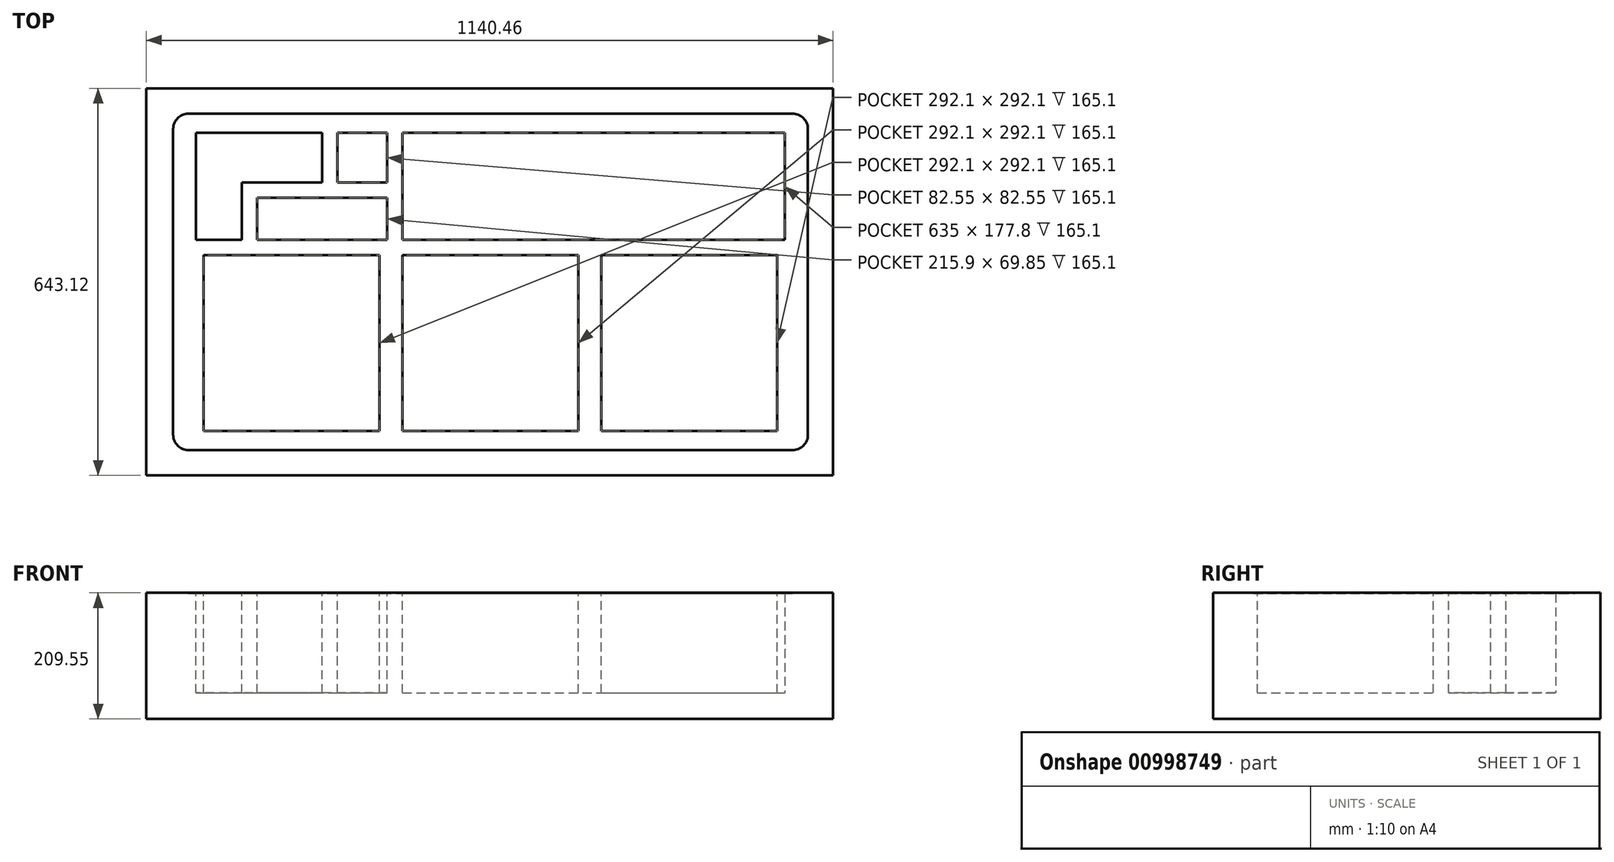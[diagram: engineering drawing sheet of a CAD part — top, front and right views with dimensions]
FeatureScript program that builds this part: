
annotation { "Feature Type Name" : "Feature", "Feature Type Description" : "" }
export const myFeature = defineFeature(function(context is Context, id is Id, definition is map)
    precondition{}
    {
        {
            var Q0;
            Q0=qCreatedBy(makeId("Top.planeOp"),FACE);
            var sketch = newSketch(context, id + "F0", { "sketchPlane" : qUnion([Q0])});
            skLineSegment(sketch, "E0.bottom", {"start": v(-44.45, -42.16) * mm, "end": v(1096, -42.16) * mm});
            skLineSegment(sketch, "E0.top", {"start": v(-44.45, 600.96) * mm, "end": v(1096, 600.96) * mm});
            skLineSegment(sketch, "E0.left", {"start": v(-44.45, -42.16) * mm, "end": v(-44.45, 600.96) * mm});
            skLineSegment(sketch, "E0.right", {"start": v(1096, -42.16) * mm, "end": v(1096, 600.96) * mm});
            skSolve(sketch);
        }
        {
            var Q0;
            Q0=makeQuery(id+"F0.imprint","IMPRINT",FACE,{"disambiguationData":[TD([[makeQuery(id+"F0.imprint","IMPRINT",EDGE,{"derivedFrom":sQuery(id+"F0.wireOp",EDGE,"E0.bottom")}),1.0]])]});
            extrude(context, id + "F1", {"entities" : qUnion([Q0]), "depth" : 209.55 * mm, "offsetDistance" : 25.4 * mm});
        }
        {
            var Q0;
            Q0=makeQuery(id+"F1.opExtrude","CAP_FACE",FACE,{"disambiguationData":[OSD([sQuery(id+"F0.wireOp",EDGE,"E0.bottom"),sQuery(id+"F0.wireOp",EDGE,"E0.top"),sQuery(id+"F0.wireOp",EDGE,"E0.left"),sQuery(id+"F0.wireOp",EDGE,"E0.right")])],"isStart":false});
            var sketch = newSketch(context, id + "F2", { "sketchPlane" : qUnion([Q0])});
            skLineSegment(sketch, "E1.bottom", {"start": v(25.4, 0) * mm, "end": v(1028.7, 0) * mm});
            skLineSegment(sketch, "E1.top", {"start": v(25.4, 558.8) * mm, "end": v(1028.7, 558.8) * mm});
            skLineSegment(sketch, "E1.left", {"start": v(0, 25.4) * mm, "end": v(0, 533.4) * mm});
            skLineSegment(sketch, "E1.right", {"start": v(1054.1, 25.4) * mm, "end": v(1054.1, 533.4) * mm});
            skPoint(sketch, "E2.visualSharp", {"position": v(0, 558.8) * mm});
            skArc(sketch, "E2.filletArc", {"start": v(25.4, 558.8) * mm, "mid": v(7.44, 551.36) * mm, "end": v(0, 533.4) * mm});
            skPoint(sketch, "E3.visualSharp", {"position": v(1054.1, 558.8) * mm});
            skArc(sketch, "E3.filletArc", {"start": v(1054.1, 533.4) * mm, "mid": v(1046.66, 551.36) * mm, "end": v(1028.7, 558.8) * mm});
            skPoint(sketch, "E4.visualSharp", {"position": v(1054.1, 0) * mm});
            skArc(sketch, "E4.filletArc", {"start": v(1028.7, 0) * mm, "mid": v(1046.66, 7.44) * mm, "end": v(1054.1, 25.4) * mm});
            skPoint(sketch, "E5.visualSharp", {"position": v(0, 0) * mm});
            skArc(sketch, "E5.filletArc", {"start": v(0, 25.4) * mm, "mid": v(7.44, 7.44) * mm, "end": v(25.4, 0) * mm});
            skSolve(sketch);
        }
        {
            var Q0;
            Q0=makeQuery(id+"F2.imprint","IMPRINT",FACE,{"disambiguationData":[TD([[makeQuery(id+"F2.imprint","IMPRINT",EDGE,{"derivedFrom":sQuery(id+"F2.wireOp",EDGE,"E1.bottom")}),1.0]])]});
            extrude(context, id + "F3", {"entities" : qUnion([Q0]), "operationType" : NewBodyOperationType.REMOVE, "oppositeDirection" : true, "depth" : 191.77 * mm, "offsetDistance" : 25.4 * mm});
        }
        {
            var Q0;
            Q0=makeQuery(id+"F3.boolean.opBoolean","COPY",FACE,{"derivedFrom":makeQuery(id+"F3.opExtrude","CAP_FACE",FACE,{"disambiguationData":[OSD([sQuery(id+"F2.wireOp",EDGE,"E1.bottom"),sQuery(id+"F2.wireOp",EDGE,"E1.top"),sQuery(id+"F2.wireOp",EDGE,"E1.left"),sQuery(id+"F2.wireOp",EDGE,"E1.right"),sQuery(id+"F2.wireOp",EDGE,"E2.filletArc"),sQuery(id+"F2.wireOp",EDGE,"E3.filletArc"),sQuery(id+"F2.wireOp",EDGE,"E4.filletArc"),sQuery(id+"F2.wireOp",EDGE,"E5.filletArc")])],"isStart":false})});
            var sketch = newSketch(context, id + "F4", { "sketchPlane" : qUnion([Q0])});
            skLineSegment(sketch, "E6.bottom", {"start": v(38.1, 31.75) * mm, "end": v(1016, 31.75) * mm});
            skLineSegment(sketch, "E6.top", {"start": v(38.1, 527.05) * mm, "end": v(1016, 527.05) * mm});
            skLineSegment(sketch, "E6.left", {"start": v(38.1, 31.75) * mm, "end": v(38.1, 527.05) * mm});
            skLineSegment(sketch, "E6.right", {"start": v(1016, 31.75) * mm, "end": v(1016, 527.05) * mm});
            skLineSegment(sketch, "E7.bottom", {"start": v(25.4, 0) * mm, "end": v(1028.7, 0) * mm});
            skLineSegment(sketch, "E7.top", {"start": v(25.4, 558.8) * mm, "end": v(1028.7, 558.8) * mm});
            skLineSegment(sketch, "E7.left", {"start": v(0, 25.4) * mm, "end": v(0, 533.4) * mm});
            skLineSegment(sketch, "E7.right", {"start": v(1054.1, 25.4) * mm, "end": v(1054.1, 533.4) * mm});
            skPoint(sketch, "E8.visualSharp", {"position": v(0, 558.8) * mm});
            skArc(sketch, "E8.filletArc", {"start": v(25.4, 558.8) * mm, "mid": v(7.44, 551.36) * mm, "end": v(0, 533.4) * mm});
            skPoint(sketch, "E9.visualSharp", {"position": v(0, 0) * mm});
            skArc(sketch, "E9.filletArc", {"start": v(0, 25.4) * mm, "mid": v(7.44, 7.44) * mm, "end": v(25.4, 0) * mm});
            skPoint(sketch, "E10.visualSharp", {"position": v(1054.1, 0) * mm});
            skArc(sketch, "E10.filletArc", {"start": v(1028.7, 0) * mm, "mid": v(1046.66, 7.44) * mm, "end": v(1054.1, 25.4) * mm});
            skPoint(sketch, "E11.visualSharp", {"position": v(1054.1, 558.8) * mm});
            skArc(sketch, "E11.filletArc", {"start": v(1054.1, 533.4) * mm, "mid": v(1046.66, 551.36) * mm, "end": v(1028.7, 558.8) * mm});
            skSolve(sketch);
        }
        {
            var Q0;
            Q0 = qSketchRegion(id + "F4", true);
            extrude(context, id + "F5", {"entities" : qUnion([Q0]), "operationType" : NewBodyOperationType.ADD, "depth" : 190.5 * mm, "offsetDistance" : 25.4 * mm});
        }
        {
            var Q0;
            Q0=makeQuery(id+"F3.boolean.opBoolean","COPY",FACE,{"derivedFrom":makeQuery(id+"F3.opExtrude","CAP_FACE",FACE,{"disambiguationData":[OSD([sQuery(id+"F2.wireOp",EDGE,"E1.bottom"),sQuery(id+"F2.wireOp",EDGE,"E1.top"),sQuery(id+"F2.wireOp",EDGE,"E1.left"),sQuery(id+"F2.wireOp",EDGE,"E1.right"),sQuery(id+"F2.wireOp",EDGE,"E2.filletArc"),sQuery(id+"F2.wireOp",EDGE,"E3.filletArc"),sQuery(id+"F2.wireOp",EDGE,"E4.filletArc"),sQuery(id+"F2.wireOp",EDGE,"E5.filletArc")])],"isStart":false})});
            extrude(context, id + "F6", {"entities" : qUnion([Q0]), "operationType" : NewBodyOperationType.ADD, "depth" : 25.4 * mm, "offsetDistance" : 25.4 * mm});
        }
        {
            var Q0;
            Q0=makeQuery(id+"F5.opExtrude","CAP_FACE",FACE,{"disambiguationData":[OSD([sQuery(id+"F4.wireOp",EDGE,"E6.bottom"),sQuery(id+"F4.wireOp",EDGE,"E6.top"),sQuery(id+"F4.wireOp",EDGE,"E6.left"),sQuery(id+"F4.wireOp",EDGE,"E6.right"),sQuery(id+"F4.wireOp",EDGE,"E7.bottom"),sQuery(id+"F4.wireOp",EDGE,"E7.top"),sQuery(id+"F4.wireOp",EDGE,"E7.left"),sQuery(id+"F4.wireOp",EDGE,"E7.right"),sQuery(id+"F4.wireOp",EDGE,"E8.filletArc"),sQuery(id+"F4.wireOp",EDGE,"E9.filletArc"),sQuery(id+"F4.wireOp",EDGE,"E10.filletArc"),sQuery(id+"F4.wireOp",EDGE,"E11.filletArc")])],"isStart":false});
            var sketch = newSketch(context, id + "F7", { "sketchPlane" : qUnion([Q0])});
            skLineSegment(sketch, "E12.bottom", {"start": v(1016, 31.75) * mm, "end": v(1003.3, 31.75) * mm});
            skLineSegment(sketch, "E12.left", {"start": v(1016, 31.75) * mm, "end": v(1016, 323.85) * mm});
            skLineSegment(sketch, "E12.right", {"start": v(1003.3, 31.75) * mm, "end": v(1003.3, 323.85) * mm});
            skLineSegment(sketch, "E13.bottom", {"start": v(1003.3, 323.85) * mm, "end": v(711.2, 323.85) * mm});
            skLineSegment(sketch, "E13.top", {"start": v(1003.3, 31.75) * mm, "end": v(711.2, 31.75) * mm});
            skLineSegment(sketch, "E13.left", {"start": v(1003.3, 323.85) * mm, "end": v(1003.3, 31.75) * mm});
            skLineSegment(sketch, "E13.right", {"start": v(711.2, 323.85) * mm, "end": v(711.2, 31.75) * mm});
            skLineSegment(sketch, "E14.top", {"start": v(711.2, 31.75) * mm, "end": v(673.1, 31.75) * mm});
            skLineSegment(sketch, "E14.right", {"start": v(673.1, 323.85) * mm, "end": v(673.1, 31.75) * mm});
            skLineSegment(sketch, "E15.bottom", {"start": v(673.1, 323.85) * mm, "end": v(381, 323.85) * mm});
            skLineSegment(sketch, "E15.top", {"start": v(673.1, 31.75) * mm, "end": v(381, 31.75) * mm});
            skLineSegment(sketch, "E15.right", {"start": v(381, 323.85) * mm, "end": v(381, 31.75) * mm});
            skLineSegment(sketch, "E16.top", {"start": v(381, 31.75) * mm, "end": v(342.9, 31.75) * mm});
            skLineSegment(sketch, "E16.right", {"start": v(342.9, 323.85) * mm, "end": v(342.9, 31.75) * mm});
            skLineSegment(sketch, "E17.bottom", {"start": v(342.9, 323.85) * mm, "end": v(50.8, 323.85) * mm});
            skLineSegment(sketch, "E17.top", {"start": v(342.9, 31.75) * mm, "end": v(50.8, 31.75) * mm});
            skLineSegment(sketch, "E17.right", {"start": v(50.8, 323.85) * mm, "end": v(50.8, 31.75) * mm});
            skLineSegment(sketch, "E18.top", {"start": v(50.8, 31.75) * mm, "end": v(38.1, 31.75) * mm});
            skLineSegment(sketch, "E18.right", {"start": v(38.1, 323.85) * mm, "end": v(38.1, 31.75) * mm});
            skLineSegment(sketch, "E19.bottom", {"start": v(1016, 527.05) * mm, "end": v(381, 527.05) * mm});
            skLineSegment(sketch, "E19.top", {"start": v(1016, 349.25) * mm, "end": v(381, 349.25) * mm});
            skLineSegment(sketch, "E19.left", {"start": v(1016, 527.05) * mm, "end": v(1016, 349.25) * mm});
            skLineSegment(sketch, "E19.right", {"start": v(381, 527.05) * mm, "end": v(381, 349.25) * mm});
            skLineSegment(sketch, "E20.bottom", {"start": v(355.6, 527.05) * mm, "end": v(273.05, 527.05) * mm});
            skLineSegment(sketch, "E20.top", {"start": v(355.6, 444.5) * mm, "end": v(273.05, 444.5) * mm});
            skLineSegment(sketch, "E20.left", {"start": v(355.6, 527.05) * mm, "end": v(355.6, 444.5) * mm});
            skLineSegment(sketch, "E20.right", {"start": v(273.05, 527.05) * mm, "end": v(273.05, 444.5) * mm});
            skLineSegment(sketch, "E21.bottom", {"start": v(355.6, 419.1) * mm, "end": v(139.7, 419.1) * mm});
            skLineSegment(sketch, "E21.top", {"start": v(355.6, 349.25) * mm, "end": v(139.7, 349.25) * mm});
            skLineSegment(sketch, "E21.left", {"start": v(355.6, 419.1) * mm, "end": v(355.6, 349.25) * mm});
            skLineSegment(sketch, "E21.right", {"start": v(139.7, 419.1) * mm, "end": v(139.7, 349.25) * mm});
            skLineSegment(sketch, "E22.bottom", {"start": v(247.65, 527.05) * mm, "end": v(38.1, 527.05) * mm});
            skLineSegment(sketch, "E22.top", {"start": v(247.65, 444.5) * mm, "end": v(114.3, 444.5) * mm});
            skLineSegment(sketch, "E22.left", {"start": v(247.65, 527.05) * mm, "end": v(247.65, 444.5) * mm});
            skLineSegment(sketch, "E22.right", {"start": v(38.1, 527.05) * mm, "end": v(38.1, 444.5) * mm});
            skLineSegment(sketch, "E23.top", {"start": v(114.3, 349.25) * mm, "end": v(38.1, 349.25) * mm});
            skLineSegment(sketch, "E23.left", {"start": v(114.3, 444.5) * mm, "end": v(114.3, 349.25) * mm});
            skLineSegment(sketch, "E23.right", {"start": v(38.1, 444.5) * mm, "end": v(38.1, 349.25) * mm});
            skLineSegment(sketch, "E24", {"start": v(38.1, 349.25) * mm, "end": v(38.1, 323.85) * mm});
            skLineSegment(sketch, "E25", {"start": v(1016, 349.25) * mm, "end": v(1016, 323.85) * mm});
            skSolve(sketch);
        }
        {
            var Q0;
            Q0=makeQuery(id+"F7.imprint","IMPRINT",FACE,{"disambiguationData":[TD([[makeQuery(id+"F7.imprint","IMPRINT",EDGE,{"derivedFrom":sQuery(id+"F7.wireOp",EDGE,"E12.bottom")}),1.0]])]});
            extrude(context, id + "F8", {"entities" : qUnion([Q0]), "operationType" : NewBodyOperationType.ADD, "oppositeDirection" : true, "depth" : 165.1 * mm, "offsetDistance" : 25.4 * mm});
        }
    });
